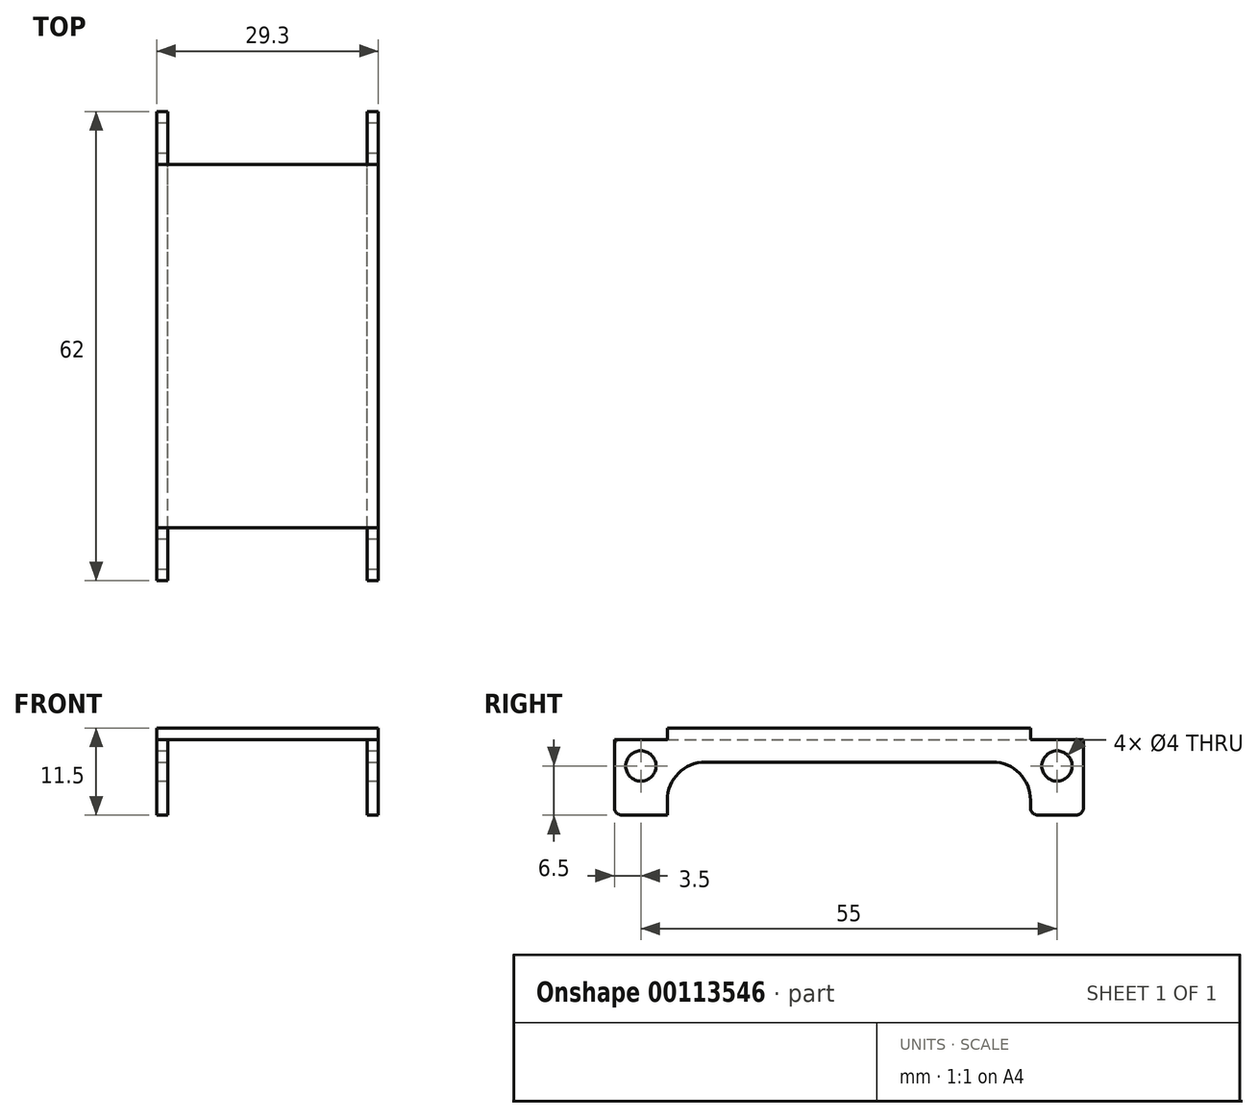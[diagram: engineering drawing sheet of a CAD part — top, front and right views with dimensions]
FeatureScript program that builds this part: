
annotation { "Feature Type Name" : "Feature", "Feature Type Description" : "" }
export const myFeature = defineFeature(function(context is Context, id is Id, definition is map)
    precondition{}
    {
        {
            var Q0;
            Q0=qCreatedBy(makeId("Front.planeOp"),FACE);
            var sketch = newSketch(context, id + "F0", { "sketchPlane" : qUnion([Q0])});
            skLineSegment(sketch, "E0.bottom", {"start": v(0, 0) * mm, "end": v(1.5, 0) * mm});
            skLineSegment(sketch, "E0.top", {"start": v(0, 11.5) * mm, "end": v(29.3, 11.5) * mm});
            skLineSegment(sketch, "E0.left", {"start": v(0, 0) * mm, "end": v(0, 11.5) * mm});
            skLineSegment(sketch, "E0.right", {"start": v(29.3, 0) * mm, "end": v(29.3, 11.5) * mm});
            skLineSegment(sketch, "E1.top", {"start": v(1.5, 10) * mm, "end": v(27.8, 10) * mm});
            skLineSegment(sketch, "E1.left", {"start": v(1.5, 0) * mm, "end": v(1.5, 10) * mm});
            skLineSegment(sketch, "E1.right", {"start": v(27.8, 0) * mm, "end": v(27.8, 10) * mm});
            skLineSegment(sketch, "E2.trimOffspring", {"start": v(27.8, 0) * mm, "end": v(29.3, 0) * mm});
            skSolve(sketch);
        }
        {
            var Q0;
            Q0=qSketchRegion(id+"F0",true);
            extrude(context, id + "F1", {"entities" : qUnion([Q0]), "depth" : 62 * mm});
        }
        {
            var Q0;
            Q0=makeQuery(id+"F1.opExtrude","SWEPT_FACE",FACE,{"disambiguationData":[OSD([sQuery(id+"F0.wireOp",EDGE,"E0.right")])]});
            var sketch = newSketch(context, id + "F2", { "sketchPlane" : qUnion([Q0])});
            skCircle(sketch, "E3", {"center": v(-58.5, 6.5) * mm, "radius": 2 * mm});
            skCircle(sketch, "E4", {"center": v(-3.5, 6.5) * mm, "radius": 2 * mm});
            skSolve(sketch);
        }
        {
            var Q0;
            Q0=qSketchRegion(id+"F2",true);
            extrude(context, id + "F3", {"entities" : qUnion([Q0]), "operationType" : NewBodyOperationType.REMOVE, "endBound" : BoundingType.THROUGH_ALL, "oppositeDirection" : true, "depth" : 25 * mm});
        }
        {
            var Q0;
            Q0=makeQuery(id+"F1.opExtrude","SWEPT_FACE",FACE,{"disambiguationData":[OSD([sQuery(id+"F0.wireOp",EDGE,"E0.right")])]});
            var sketch = newSketch(context, id + "F4", { "sketchPlane" : qUnion([Q0])});
            skPoint(sketch, "E5", {"position": v(-58.5, 6.5) * mm});
            skLineSegment(sketch, "E6.bottom", {"start": v(-7, 0) * mm, "end": v(-55, 0) * mm});
            skLineSegment(sketch, "E6.top", {"start": v(-7, 7) * mm, "end": v(-55, 7) * mm});
            skLineSegment(sketch, "E6.left", {"start": v(-7, 0) * mm, "end": v(-7, 7) * mm});
            skLineSegment(sketch, "E6.right", {"start": v(-55, 0) * mm, "end": v(-55, 7) * mm});
            skPoint(sketch, "E7", {"position": v(-3.5, 6.5) * mm});
            skSolve(sketch);
        }
        {
            var Q0;
            Q0=qSketchRegion(id+"F4",true);
            extrude(context, id + "F5", {"entities" : qUnion([Q0]), "operationType" : NewBodyOperationType.REMOVE, "endBound" : BoundingType.THROUGH_ALL, "oppositeDirection" : true, "depth" : 25 * mm});
        }
        {
            var Q0;
            Q0=makeQuery(id+"F1.opExtrude","CAP_EDGE",EDGE,{"disambiguationData":[OSD([sQuery(id+"F0.wireOp",EDGE,"E2.trimOffspring")])],"isStart":false});
            var Q1;
            Q1=makeQuery(id+"F5.boolean.opBoolean","COPY",EDGE,{"disambiguationData":[OD(0.0)],"derivedFrom":makeQuery(id+"F5.opExtrude","SWEPT_EDGE",EDGE,{"disambiguationData":[OSD([sQuery(id+"F0.wireOp",EDGE,"E0.right"),sQuery(id+"F0.wireOp",EDGE,"E2.trimOffspring"),sQuery(id+"F4.wireOp",EDGE,"E6.bottom"),sQuery(id+"F4.wireOp",EDGE,"E6.right")])]})});
            var Q2;
            Q2=makeQuery(id+"F1.opExtrude","CAP_EDGE",EDGE,{"disambiguationData":[OSD([sQuery(id+"F0.wireOp",EDGE,"E0.bottom")])],"isStart":false});
            var Q3;
            Q3=makeQuery(id+"F5.boolean.opBoolean","COPY",EDGE,{"disambiguationData":[OD(1.0)],"derivedFrom":makeQuery(id+"F5.opExtrude","SWEPT_EDGE",EDGE,{"disambiguationData":[OSD([sQuery(id+"F0.wireOp",EDGE,"E0.right"),sQuery(id+"F0.wireOp",EDGE,"E2.trimOffspring"),sQuery(id+"F4.wireOp",EDGE,"E6.bottom"),sQuery(id+"F4.wireOp",EDGE,"E6.right")])]})});
            var Q4;
            Q4=makeQuery(id+"F1.opExtrude","CAP_EDGE",EDGE,{"disambiguationData":[OSD([sQuery(id+"F0.wireOp",EDGE,"E2.trimOffspring")])],"isStart":true});
            var Q5;
            Q5=makeQuery(id+"F5.boolean.opBoolean","COPY",EDGE,{"disambiguationData":[OD(0.0)],"derivedFrom":makeQuery(id+"F5.opExtrude","SWEPT_EDGE",EDGE,{"disambiguationData":[OSD([sQuery(id+"F0.wireOp",EDGE,"E0.right"),sQuery(id+"F0.wireOp",EDGE,"E2.trimOffspring"),sQuery(id+"F4.wireOp",EDGE,"E6.bottom"),sQuery(id+"F4.wireOp",EDGE,"E6.left")])]})});
            var Q6;
            Q6=makeQuery(id+"F5.boolean.opBoolean","COPY",EDGE,{"disambiguationData":[OD(1.0)],"derivedFrom":makeQuery(id+"F5.opExtrude","SWEPT_EDGE",EDGE,{"disambiguationData":[OSD([sQuery(id+"F0.wireOp",EDGE,"E0.right"),sQuery(id+"F0.wireOp",EDGE,"E2.trimOffspring"),sQuery(id+"F4.wireOp",EDGE,"E6.bottom"),sQuery(id+"F4.wireOp",EDGE,"E6.left")])]})});
            var Q7;
            Q7=makeQuery(id+"F1.opExtrude","CAP_EDGE",EDGE,{"disambiguationData":[OSD([sQuery(id+"F0.wireOp",EDGE,"E0.bottom")])],"isStart":true});
            fillet(context, id + "F6", {"entities" : qUnion([Q0, Q1, Q2, Q3, Q4, Q5, Q6, Q7]), "radius" : 1 * mm, "tangentPropagation" : true, "allowEdgeOverflow" : false});
        }
        {
            var Q0;
            Q0=makeQuery(id+"F5.boolean.opBoolean","COPY",EDGE,{"disambiguationData":[OD(0.0)],"derivedFrom":makeQuery(id+"F5.opExtrude","SWEPT_EDGE",EDGE,{"disambiguationData":[OSD([sQuery(id+"F4.wireOp",EDGE,"E6.top"),sQuery(id+"F4.wireOp",EDGE,"E6.left")])]})});
            var Q1;
            Q1=makeQuery(id+"F5.boolean.opBoolean","COPY",EDGE,{"disambiguationData":[OD(1.0)],"derivedFrom":makeQuery(id+"F5.opExtrude","SWEPT_EDGE",EDGE,{"disambiguationData":[OSD([sQuery(id+"F4.wireOp",EDGE,"E6.top"),sQuery(id+"F4.wireOp",EDGE,"E6.left")])]})});
            var Q2;
            Q2=makeQuery(id+"F5.boolean.opBoolean","COPY",EDGE,{"disambiguationData":[OD(0.0)],"derivedFrom":makeQuery(id+"F5.opExtrude","SWEPT_EDGE",EDGE,{"disambiguationData":[OSD([sQuery(id+"F4.wireOp",EDGE,"E6.top"),sQuery(id+"F4.wireOp",EDGE,"E6.right")])]})});
            var Q3;
            Q3=makeQuery(id+"F5.boolean.opBoolean","COPY",EDGE,{"disambiguationData":[OD(1.0)],"derivedFrom":makeQuery(id+"F5.opExtrude","SWEPT_EDGE",EDGE,{"disambiguationData":[OSD([sQuery(id+"F4.wireOp",EDGE,"E6.top"),sQuery(id+"F4.wireOp",EDGE,"E6.right")])]})});
            fillet(context, id + "F7", {"entities" : qUnion([Q0, Q1, Q2, Q3]), "radius" : 5 * mm, "tangentPropagation" : true, "allowEdgeOverflow" : false});
        }
        {
            var Q0;
            Q0=makeQuery(id+"F1.opExtrude","SWEPT_FACE",FACE,{"disambiguationData":[OSD([sQuery(id+"F0.wireOp",EDGE,"E0.top")])]});
            var sketch = newSketch(context, id + "F8", { "sketchPlane" : qUnion([Q0])});
            skLineSegment(sketch, "E8", {"start": v(0, -31) * mm, "end": v(29.3, -31) * mm, "construction": true});
            skLineSegment(sketch, "E9.bottom", {"start": v(29.3, -62) * mm, "end": v(0, -62) * mm});
            skLineSegment(sketch, "E9.top", {"start": v(29.3, -55) * mm, "end": v(0, -55) * mm});
            skLineSegment(sketch, "E9.left", {"start": v(29.3, -62) * mm, "end": v(29.3, -55) * mm});
            skLineSegment(sketch, "E9.right", {"start": v(0, -62) * mm, "end": v(0, -55) * mm});
            skLineSegment(sketch, "E10.MirrorCS", {"start": v(0, 0) * mm, "end": v(0, -7) * mm});
            skLineSegment(sketch, "E11.MirrorCS", {"start": v(29.3, 0) * mm, "end": v(0, 0) * mm});
            skLineSegment(sketch, "E12.MirrorCS", {"start": v(29.3, 0) * mm, "end": v(29.3, -7) * mm});
            skLineSegment(sketch, "E13.MirrorCS", {"start": v(29.3, -7) * mm, "end": v(0, -7) * mm});
            skSolve(sketch);
        }
        {
            var Q0;
            Q0=qSketchRegion(id+"F8",true);
            extrude(context, id + "F9", {"entities" : qUnion([Q0]), "operationType" : NewBodyOperationType.REMOVE, "oppositeDirection" : true, "depth" : 1.5 * mm});
        }
        {
            var Q0;
            Q0=makeQuery(id+"F9.boolean.opBoolean","COPY",EDGE,{"disambiguationData":[OD(0.0)],"derivedFrom":makeQuery(id+"F9.opExtrude","CAP_EDGE",EDGE,{"disambiguationData":[OSD([sQuery(id+"F8.wireOp",EDGE,"E9.bottom")])],"isStart":false})});
            var Q1;
            Q1=makeQuery(id+"F9.boolean.opBoolean","COPY",EDGE,{"disambiguationData":[OD(1.0)],"derivedFrom":makeQuery(id+"F9.opExtrude","CAP_EDGE",EDGE,{"disambiguationData":[OSD([sQuery(id+"F8.wireOp",EDGE,"E9.bottom")])],"isStart":false})});
            var Q2;
            Q2=makeQuery(id+"F9.boolean.opBoolean","COPY",EDGE,{"disambiguationData":[OD(0.0)],"derivedFrom":makeQuery(id+"F9.opExtrude","CAP_EDGE",EDGE,{"disambiguationData":[OSD([sQuery(id+"F8.wireOp",EDGE,"E11.MirrorCS")])],"isStart":false})});
            var Q3;
            Q3=makeQuery(id+"F9.boolean.opBoolean","COPY",EDGE,{"disambiguationData":[OD(1.0)],"derivedFrom":makeQuery(id+"F9.opExtrude","CAP_EDGE",EDGE,{"disambiguationData":[OSD([sQuery(id+"F8.wireOp",EDGE,"E11.MirrorCS")])],"isStart":false})});
            fillet(context, id + "F10", {"entities" : qUnion([Q0, Q1, Q2, Q3]), "radius" : 1 * mm, "tangentPropagation" : true, "allowEdgeOverflow" : false});
        }
    });
